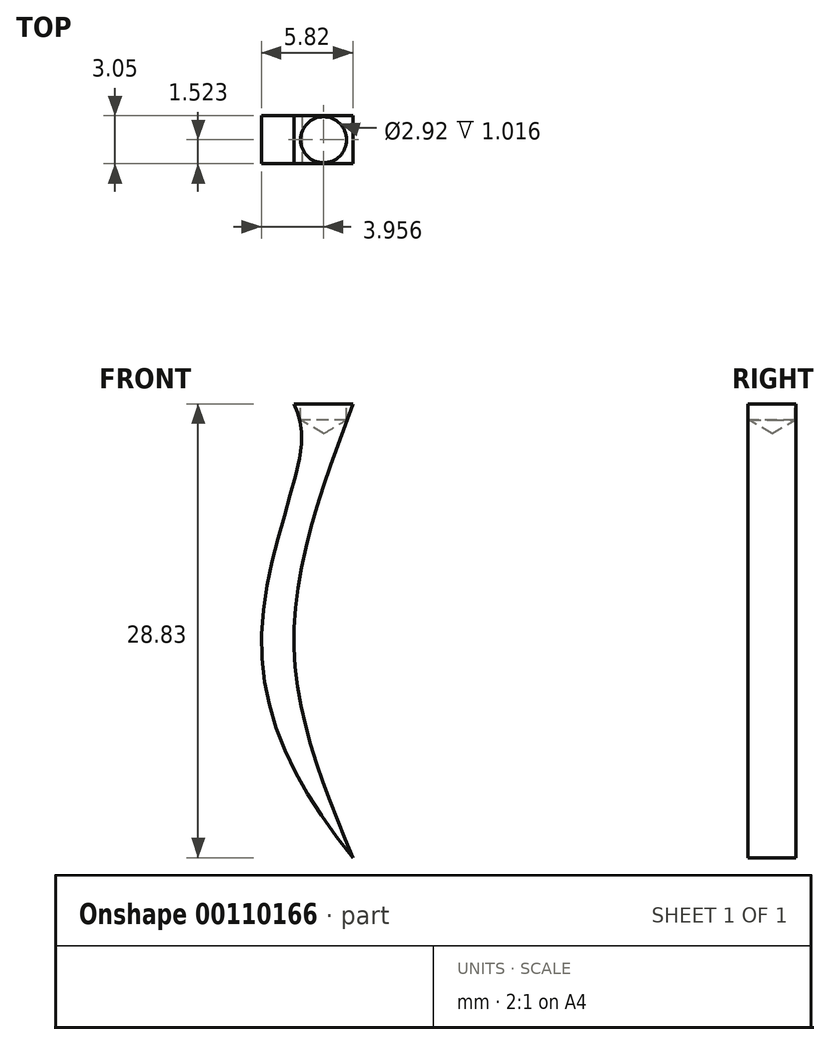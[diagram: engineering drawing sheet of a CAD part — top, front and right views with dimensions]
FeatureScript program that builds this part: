
annotation { "Feature Type Name" : "Feature", "Feature Type Description" : "" }
export const myFeature = defineFeature(function(context is Context, id is Id, definition is map)
    precondition{}
    {
        {
            var Q0;
            Q0=qCreatedBy(makeId("Front.planeOp"),FACE);
            var sketch = newSketch(context, id + "F0", { "sketchPlane" : qUnion([Q0])});
            skLineSegment(sketch, "E0", {"start": v(-25.45, 0) * mm, "end": v(-21.7, 0) * mm});
            skPoint(sketch, "E1.1.internal.snap0", {"position": v(-23.57, 0) * mm});
            skFitSpline(sketch, "E2", {"points": [v(-21.7, 0) * mm, v(-25.45, -15.23) * mm, v(-21.7, -28.83) * mm], "startDerivative": vector(-11.16, -30.12) * mm, "endDerivative": vector(11.36, -27.51) * mm});
            skFitSpline(sketch, "E3", {"points": [v(-21.7, -28.83) * mm, v(-27.51, -14.85) * mm, v(-24.98, -2.76) * mm, v(-25.45, 0) * mm], "startDerivative": vector(-24.72, 30.4) * mm, "endDerivative": vector(-5.69, 12.28) * mm});
            skLineSegment(sketch, "E4", {"start": v(-21.7, 0) * mm, "end": v(-21.42, 0.5) * mm});
            skLineSegment(sketch, "E5", {"start": v(-25.45, 0) * mm, "end": v(-25.7, 0.54) * mm});
            skPoint(sketch, "E6", {"position": v(-23.62, -0.1) * mm});
            skSolve(sketch);
        }
        {
            var Q0;
            Q0 = qSketchRegion(id + "F0", true);
            extrude(context, id + "F1", {"entities" : qUnion([Q0]), "oppositeDirection" : true, "depth" : 3.05 * mm});
        }
        {
            var Q0;
            Q0=qCreatedBy(makeId("Top.planeOp"),FACE);
            var sketch = newSketch(context, id + "F2", { "sketchPlane" : qUnion([Q0])});
            skPoint(sketch, "E7", {"position": v(-23.56, 1.52) * mm});
            skSolve(sketch);
        }
        {
            var Q0;
            Q0=sQuery(id+"F2.wireOp",VERTEX,"E7");
            var Q1;
            Q1=makeQuery(id+"F1.opExtrude","SWEPT_BODY",BODY,{"disambiguationData":[OSD([sQuery(id+"F0.wireOp",EDGE,"E0"),sQuery(id+"F0.wireOp",EDGE,"E2"),sQuery(id+"F0.wireOp",EDGE,"E3")])]});
            hole(context, id + "F3", {"style" : HoleStyle.SIMPLE, "endStyle" : HoleEndStyle.BLIND, "holeDiameter" : 2.92 * mm, "holeDepth" : 1.02 * mm, "locations" : qUnion([Q0]), "scope" : qUnion([Q1])});
        }
    });
